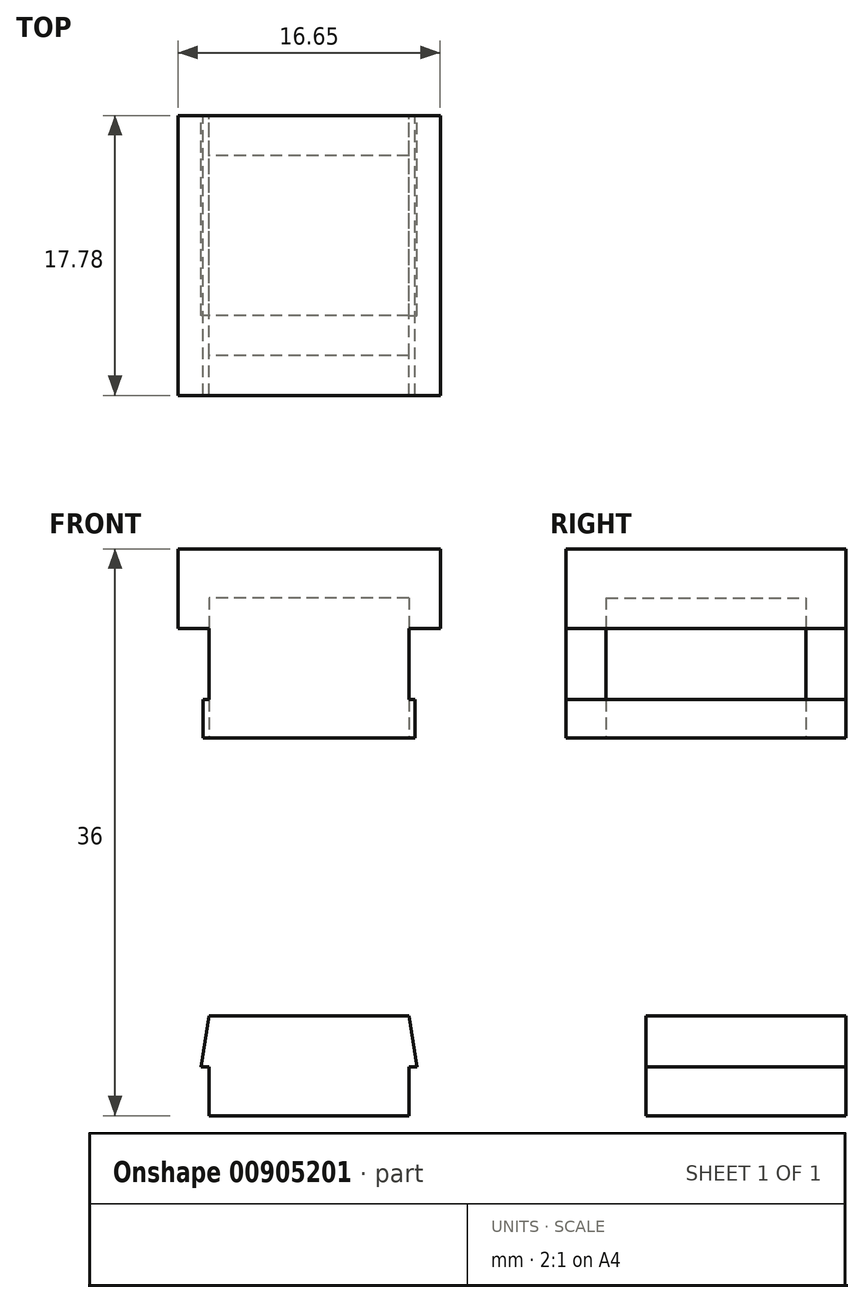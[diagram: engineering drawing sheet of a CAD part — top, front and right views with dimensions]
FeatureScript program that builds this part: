
annotation { "Feature Type Name" : "Feature", "Feature Type Description" : "" }
export const myFeature = defineFeature(function(context is Context, id is Id, definition is map)
    precondition{}
    {
        {
            var Q0;
            Q0=qCreatedBy(makeId("Front.planeOp"),FACE);
            var sketch = newSketch(context, id + "F0", { "sketchPlane" : qUnion([Q0])});
            skLineSegment(sketch, "E0", {"start": v(0, 0) * mm, "end": v(-12.7, 0) * mm});
            skLineSegment(sketch, "E1", {"start": v(-12.7, 0) * mm, "end": v(-12.7, 3.08) * mm});
            skLineSegment(sketch, "E2", {"start": v(-12.7, 6.35) * mm, "end": v(0, 6.35) * mm});
            skLineSegment(sketch, "E3", {"start": v(0, 3.08) * mm, "end": v(0, 0) * mm});
            skLineSegment(sketch, "E4", {"start": v(-12.7, 6.35) * mm, "end": v(-13.2, 3.08) * mm});
            skLineSegment(sketch, "E5", {"start": v(-13.2, 3.08) * mm, "end": v(-12.7, 3.08) * mm});
            skLineSegment(sketch, "E6", {"start": v(0, 3.08) * mm, "end": v(0.5, 3.08) * mm});
            skLineSegment(sketch, "E7", {"start": v(0.5, 3.08) * mm, "end": v(0, 6.35) * mm});
            skSolve(sketch);
        }
        {
            var Q0;
            Q0 = qSketchRegion(id + "F0", true);
            extrude(context, id + "F1", {"entities" : qUnion([Q0]), "depth" : 12.7 * mm, "offsetDistance" : 25.4 * mm});
        }
        {
            var Q0;
            Q0=qCreatedBy(makeId("Front.planeOp"),FACE);
            var sketch = newSketch(context, id + "F2", { "sketchPlane" : qUnion([Q0])});
            skLineSegment(sketch, "E8.MirrorCS", {"start": v(0, 24) * mm, "end": v(-12.7, 24) * mm});
            skLineSegment(sketch, "E9.MirrorCS", {"start": v(-12.7, 24) * mm, "end": v(-13.08, 24) * mm});
            skLineSegment(sketch, "E10.MirrorCS", {"start": v(0, 24) * mm, "end": v(0.38, 24) * mm});
            skPoint(sketch, "E11.end.orphan", {"position": v(1.98, 6.94) * mm});
            skPoint(sketch, "E12.end.orphan", {"position": v(-14.67, 6.94) * mm});
            skPoint(sketch, "E12.start.orphan", {"position": v(-12.7, 6.94) * mm});
            skPoint(sketch, "E13.end.orphan", {"position": v(-12.7, 2.43) * mm});
            skPoint(sketch, "E13.start.orphan", {"position": v(-14.67, 2.43) * mm});
            skPoint(sketch, "E14.end.orphan", {"position": v(-14.67, 0) * mm});
            skPoint(sketch, "E15.end.orphan", {"position": v(0, 6.94) * mm});
            skPoint(sketch, "E15.start.orphan", {"position": v(0, 2.43) * mm});
            skPoint(sketch, "E16.end.orphan", {"position": v(1.98, 2.43) * mm});
            skPoint(sketch, "E17.end.orphan", {"position": v(-12.7, 0) * mm});
            skPoint(sketch, "E18.end.orphan", {"position": v(1.98, 0) * mm});
            skPoint(sketch, "E18.start.orphan", {"position": v(0, 0) * mm});
            skLineSegment(sketch, "E19.MirrorCS", {"start": v(0, 26.43) * mm, "end": v(0.38, 26.43) * mm});
            skLineSegment(sketch, "E20.MirrorCS", {"start": v(0, 26.43) * mm, "end": v(0, 30.94) * mm});
            skLineSegment(sketch, "E21.MirrorCS", {"start": v(0, 30.94) * mm, "end": v(1.98, 30.94) * mm});
            skLineSegment(sketch, "E22.MirrorCS", {"start": v(1.98, 30.94) * mm, "end": v(1.98, 36) * mm});
            skLineSegment(sketch, "E23.MirrorCS", {"start": v(-14.67, 36) * mm, "end": v(1.98, 36) * mm});
            skLineSegment(sketch, "E24.MirrorCS", {"start": v(-14.67, 30.94) * mm, "end": v(-14.67, 36) * mm});
            skLineSegment(sketch, "E25.MirrorCS", {"start": v(-12.7, 30.94) * mm, "end": v(-14.67, 30.94) * mm});
            skLineSegment(sketch, "E26.MirrorCS", {"start": v(-12.7, 26.43) * mm, "end": v(-12.7, 30.94) * mm});
            skPoint(sketch, "E27.MirrorCS.end.orphan", {"position": v(-14.67, 21.57) * mm});
            skPoint(sketch, "E27.MirrorCS.start.orphan", {"position": v(-14.67, 24) * mm});
            skPoint(sketch, "E28.MirrorCS.end.orphan", {"position": v(-14.3, 21.57) * mm});
            skPoint(sketch, "E29.MirrorCS.end.orphan", {"position": v(-12.7, 17.06) * mm});
            skPoint(sketch, "E29.MirrorCS.start.orphan", {"position": v(-12.7, 21.57) * mm});
            skPoint(sketch, "E30.MirrorCS.end.orphan", {"position": v(-14.67, 12) * mm});
            skPoint(sketch, "E30.MirrorCS.start.orphan", {"position": v(-14.67, 17.06) * mm});
            skPoint(sketch, "E31.end.orphan", {"position": v(1.98, 12) * mm});
            skPoint(sketch, "E32.MirrorCS.start.orphan", {"position": v(1.98, 17.06) * mm});
            skPoint(sketch, "E33.MirrorCS.end.orphan", {"position": v(0, 17.06) * mm});
            skPoint(sketch, "E33.MirrorCS.start.orphan", {"position": v(0, 21.57) * mm});
            skPoint(sketch, "E34.MirrorCS.end.orphan", {"position": v(0.38, 21.57) * mm});
            skPoint(sketch, "E35.MirrorCS.end.orphan", {"position": v(1.98, 21.57) * mm});
            skPoint(sketch, "E35.MirrorCS.start.orphan", {"position": v(1.98, 24) * mm});
            skLineSegment(sketch, "E36", {"start": v(0.38, 26.43) * mm, "end": v(0.38, 24) * mm});
            skPoint(sketch, "E37.MirrorCS.end.orphan", {"position": v(1.98, 26.43) * mm});
            skLineSegment(sketch, "E38", {"start": v(-12.7, 26.43) * mm, "end": v(-13.08, 26.43) * mm});
            skLineSegment(sketch, "E39", {"start": v(-13.08, 26.43) * mm, "end": v(-13.08, 24) * mm});
            skPoint(sketch, "E40.MirrorCS.end.orphan", {"position": v(-14.3, 26.43) * mm});
            skPoint(sketch, "E40.MirrorCS.start.orphan", {"position": v(-14.67, 26.43) * mm});
            skSolve(sketch);
        }
        {
            var Q0;
            Q0 = qSketchRegion(id + "F2", true);
            extrude(context, id + "F3", {"entities" : qUnion([Q0]), "depth" : 17.78 * mm, "offsetDistance" : 25.4 * mm});
        }
        {
            var Q0;
            Q0=makeQuery(id+"F3.opExtrude","SWEPT_FACE",FACE,{"disambiguationData":[OSD([sQuery(id+"F2.wireOp",EDGE,"E8.MirrorCS"),sQuery(id+"F2.wireOp",EDGE,"E10.MirrorCS"),sQuery(id+"F2.wireOp",EDGE,"E9.MirrorCS")])]});
            var sketch = newSketch(context, id + "F4", { "sketchPlane" : qUnion([Q0])});
            skLineSegment(sketch, "E41.bottom", {"start": v(0, 15.24) * mm, "end": v(-12.7, 15.24) * mm});
            skLineSegment(sketch, "E41.top", {"start": v(0, 2.54) * mm, "end": v(-12.7, 2.54) * mm});
            skLineSegment(sketch, "E41.left", {"start": v(0, 15.24) * mm, "end": v(0, 2.54) * mm});
            skLineSegment(sketch, "E41.right", {"start": v(-12.7, 15.24) * mm, "end": v(-12.7, 2.54) * mm});
            skPoint(sketch, "E41.middle", {"position": v(-6.35, 8.9) * mm});
            skPoint(sketch, "E41.middle.positionSnap0", {"position": v(0.38, 8.9) * mm});
            skPoint(sketch, "E41.middle.positionSnap1", {"position": v(-6.35, 17.78) * mm});
            skPoint(sketch, "E41.centerSnap0", {"position": v(0.38, 8.9) * mm});
            skPoint(sketch, "E41.centerSnap1", {"position": v(-6.35, 17.78) * mm});
            skSolve(sketch);
        }
        {
            var Q0;
            Q0 = qSketchRegion(id + "F4", true);
            extrude(context, id + "F5", {"entities" : qUnion([Q0]), "operationType" : NewBodyOperationType.REMOVE, "oppositeDirection" : true, "depth" : 8.9 * mm, "offsetDistance" : 25.4 * mm});
        }
    });
